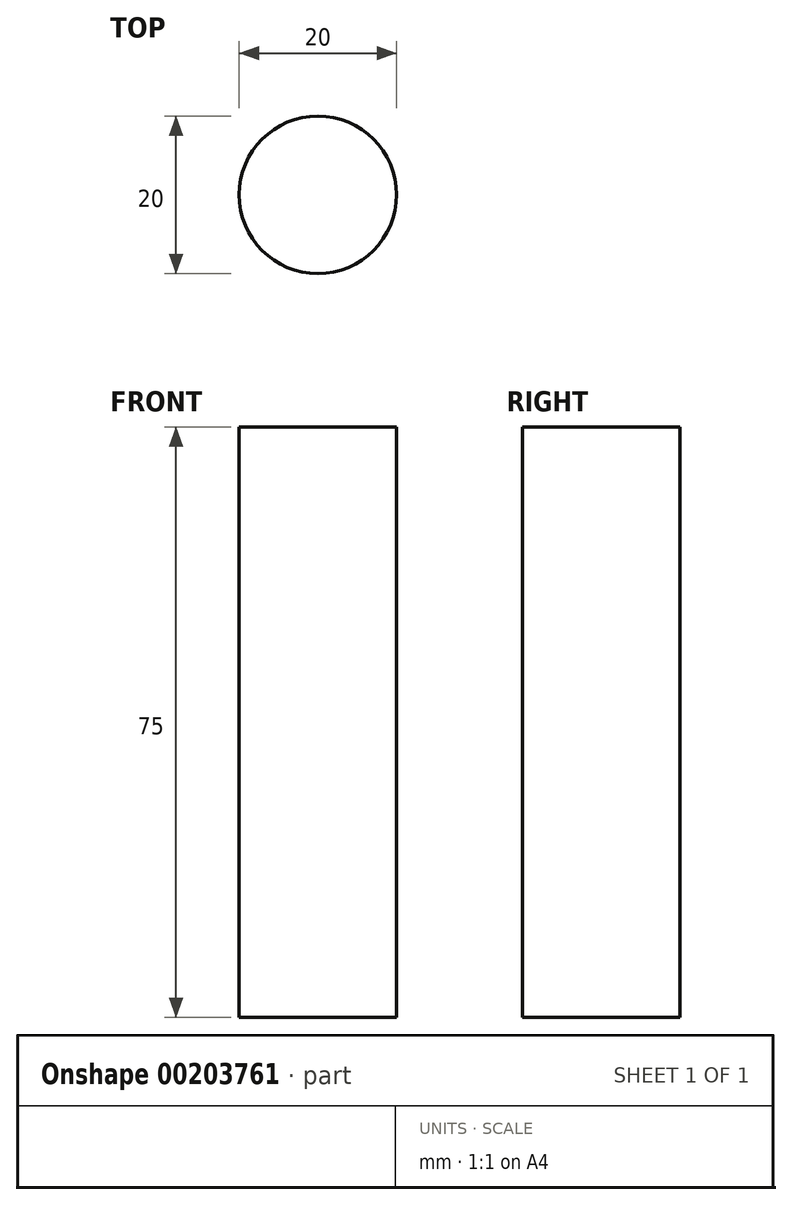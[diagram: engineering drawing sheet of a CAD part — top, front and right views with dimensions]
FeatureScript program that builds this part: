
annotation { "Feature Type Name" : "Feature", "Feature Type Description" : "" }
export const myFeature = defineFeature(function(context is Context, id is Id, definition is map)
    precondition{}
    {
        {
            var Q0;
            Q0=qCreatedBy(makeId("Top.planeOp"),FACE);
            var sketch = newSketch(context, id + "F0", { "sketchPlane" : qUnion([Q0])});
            skCircle(sketch, "E0", {"center": v(0, 0) * mm, "radius": 10 * mm});
            skSolve(sketch);
        }
        {
            var Q0;
            Q0=makeQuery(id+"F0.imprint","IMPRINT",FACE,{"disambiguationData":[TD([[makeQuery(id+"F0.imprint","IMPRINT",EDGE,{"derivedFrom":sQuery(id+"F0.wireOp",EDGE,"E0")}),1.0]])]});
            extrude(context, id + "F1", {"entities" : qUnion([Q0]), "depth" : 75 * mm});
        }
    });
